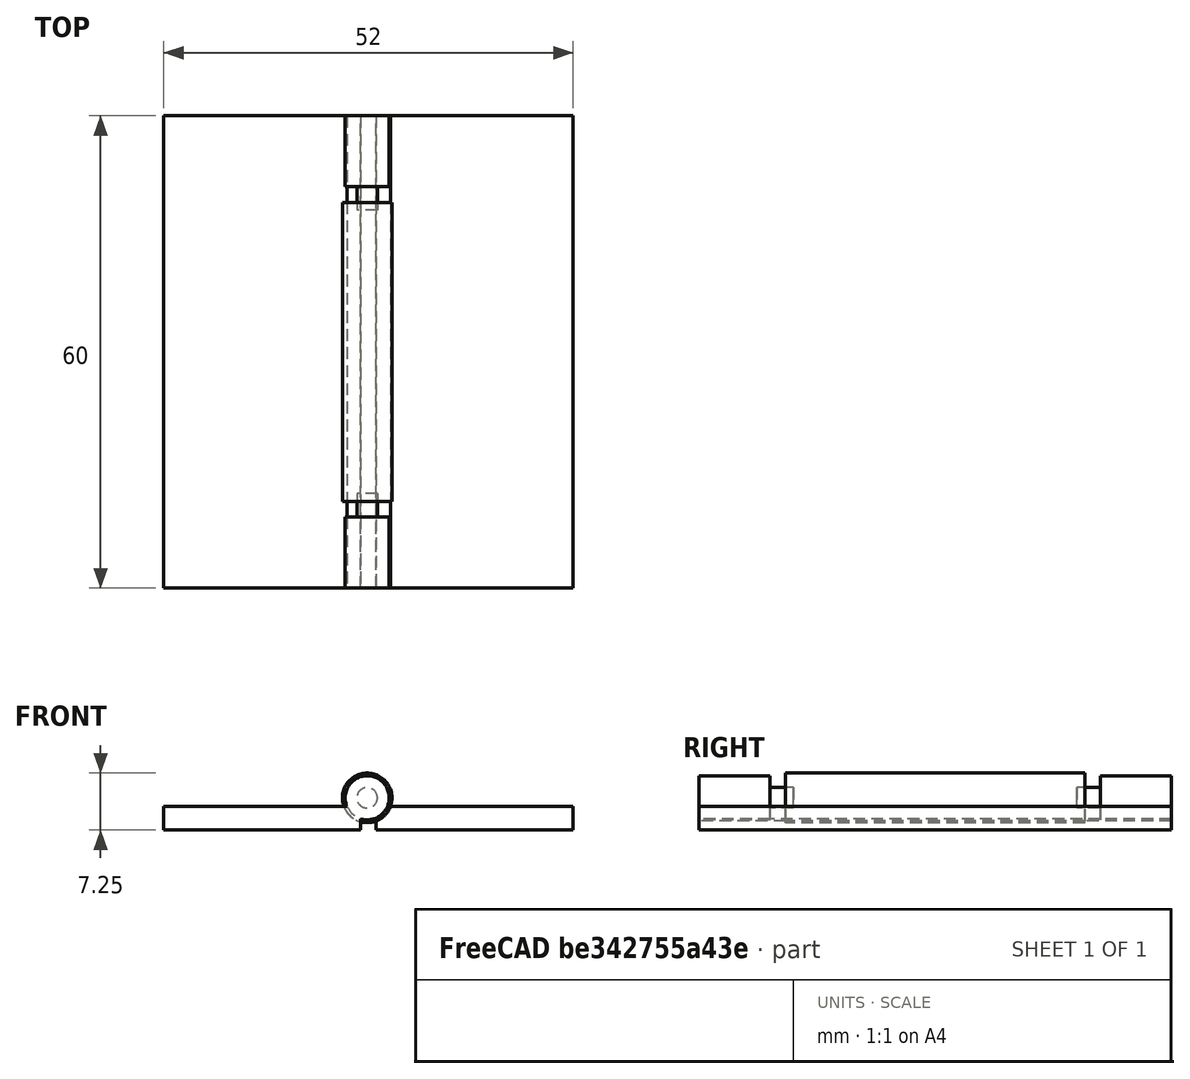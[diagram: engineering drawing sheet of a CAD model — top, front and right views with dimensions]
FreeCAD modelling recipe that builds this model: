
FCSTD DOCUMENT  (FreeCAD 0.16R6712 (Git))
Label: Hinge04
License: All rights reserved
LicenseURL: http://en.wikipedia.org/wiki/All_rights_reserved
objects: Part::Cylinder×8, Part::Cut×3, Part::MultiFuse×3, Part::Box×2, Part::Fuse×1
note: 17 computed .brp shape members not serialized (recipe doc carries the construction recipe); baked Part::Feature solids carry a one-line shape summary decoded from their .brp

FEATURE [Part::Box] Box  label="Cube"
  Height = 3
  Length = 25
  Placement = pos=(2.3,0,-1) rot=(0,0,1;0rad)
  Width = 60
FEATURE [Part::Cylinder] Cylinder
  Angle = 360
  Height = 38
  Placement = pos=(28.15,49,3.1) rot=(1,0,0;1.5708rad)
  Radius = 3.15
FEATURE [Part::Cylinder] Cylinder001
  Angle = 360
  Height = 38
  Placement = pos=(77.0984,2.91904,17.7964) rot=(0.081096,0.990566,-0.110461;1.29292rad)
  Radius = 1.5
FEATURE [Part::Cylinder] Cylinder002
  Angle = 360
  Height = 60
  Placement = pos=(28.15,60,3.1) rot=(1,0,0;1.5708rad)
  Radius = 3.15
FEATURE [Part::Cut] Cut001
  Base = -> Cylinder
  Tool = -> Cylinder001
FEATURE [Part::Box] Box001  label="Cube001"
  Height = 3
  Length = 25
  Placement = pos=(29.3,0,-1) rot=(0,0,1;0rad)
  Width = 60
FEATURE [Part::Cut] Cut
  Base = -> Box001
  Tool = -> Cylinder002
FEATURE [Part::Cylinder] Cylinder003
  Angle = 360
  Height = 60
  Placement = pos=(28.2,60,3.1) rot=(1,0,0;1.5708rad)
  Radius = 2.8
FEATURE [Part::Cut] Cut002
  Base = -> Box
  Tool = -> Cylinder003
FEATURE [Part::Cylinder] Cylinder004
  Angle = 360
  Height = 9
  Placement = pos=(28.15,9,3.1) rot=(1,0,0;1.5708rad)
  Radius = 2.8
FEATURE [Part::Cylinder] Cylinder005
  Angle = 360
  Height = 9
  Placement = pos=(28.15,60,3.1) rot=(1,0,0;1.5708rad)
  Radius = 2.8
FEATURE [Part::Cylinder] Cylinder006
  Angle = 360
  Height = 12
  Placement = pos=(28.15,12,3.1) rot=(1,0,0;1.5708rad)
  Radius = 1.3
FEATURE [Part::Cylinder] Cylinder007
  Angle = 360
  Height = 12
  Placement = pos=(28.15,60,3.1) rot=(1,0,0;1.5708rad)
  Radius = 1.3
FEATURE [Part::Fuse] Fusion
  Base = -> Cylinder005
  Tool = -> Cylinder007
FEATURE [Part::MultiFuse] Fusion001
  Shapes = -> [Cylinder006,Cylinder004]
FEATURE [Part::MultiFuse] Fusion002
  Shapes = -> [Fusion001,Fusion,Cut002]
FEATURE [Part::MultiFuse] Fusion003
  Shapes = -> [Cut,Cut001]
